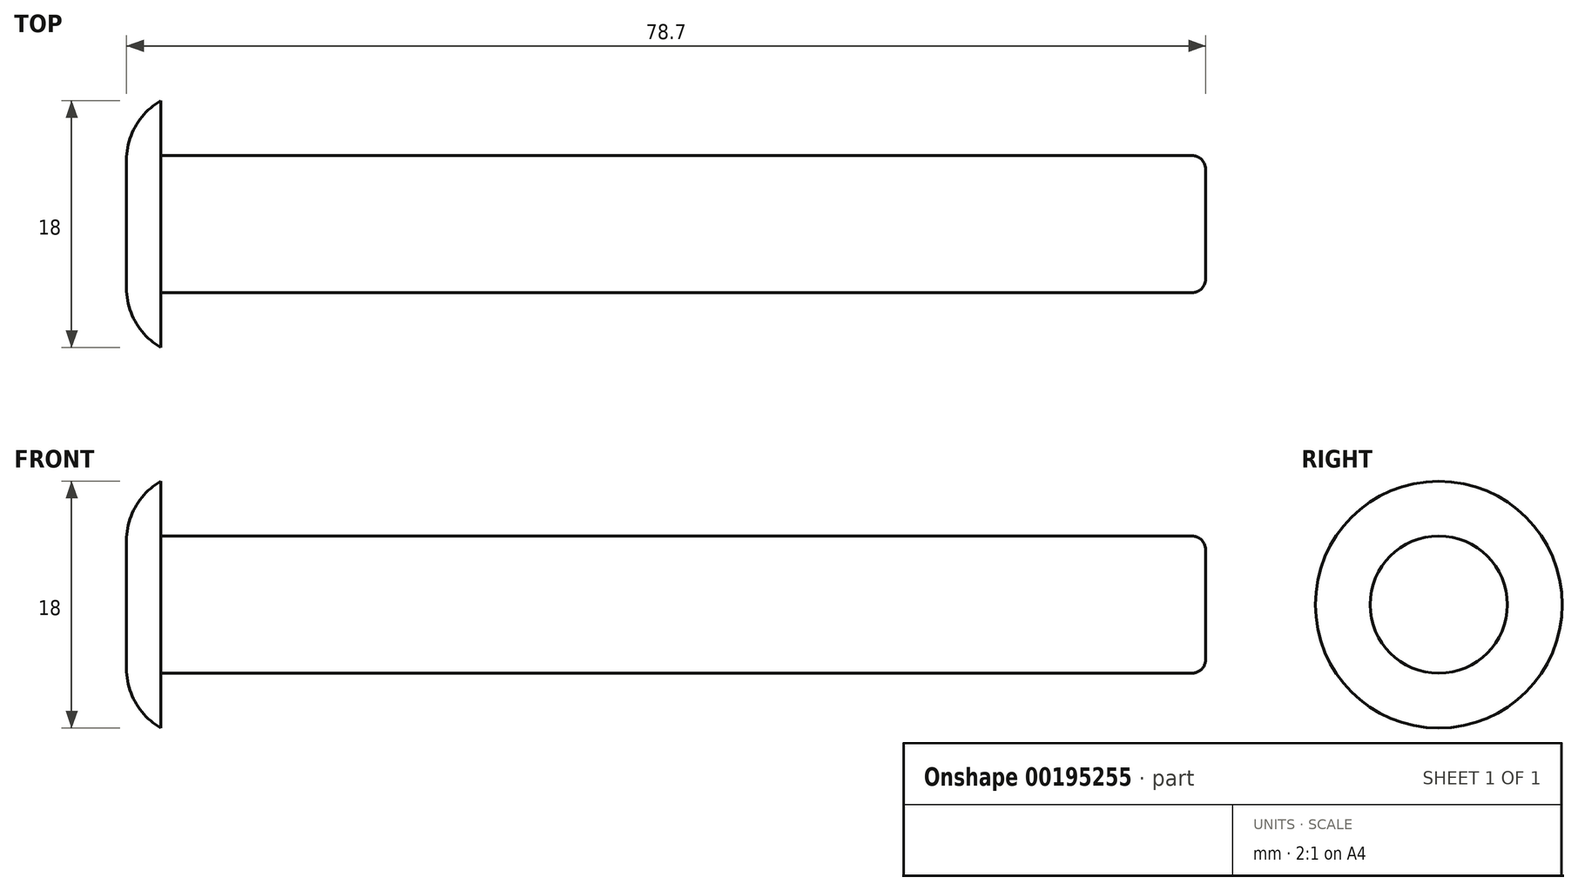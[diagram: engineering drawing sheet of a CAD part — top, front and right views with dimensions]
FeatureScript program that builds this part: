
annotation { "Feature Type Name" : "Feature", "Feature Type Description" : "" }
export const myFeature = defineFeature(function(context is Context, id is Id, definition is map)
    precondition{}
    {
        {
            var Q0;
            Q0=qCreatedBy(makeId("Right.planeOp"),FACE);
            var sketch = newSketch(context, id + "F0", { "sketchPlane" : qUnion([Q0])});
            skLineSegment(sketch, "E0", {"start": v(-18, 47.71) * mm, "end": v(-18, -27) * mm, "construction": true});
            skLineSegment(sketch, "E1", {"start": v(-18, -27) * mm, "end": v(0, -27) * mm, "construction": true});
            skLineSegment(sketch, "E2", {"start": v(0, -27) * mm, "end": v(0, -9) * mm, "construction": true});
            skLineSegment(sketch, "E3", {"start": v(0, -9) * mm, "end": v(0, 0) * mm, "construction": true});
            skCircle(sketch, "E4", {"center": v(0, 0) * mm, "radius": 9 * mm, "construction": true});
            skCircle(sketch, "E5", {"center": v(0, 0) * mm, "radius": 5 * mm});
            skSolve(sketch);
        }
        {
            var Q0;
            Q0=qCreatedBy(makeId("Right.planeOp"),FACE);
            var sketch = newSketch(context, id + "F1", { "sketchPlane" : qUnion([Q0])});
            skCircle(sketch, "E6.0", {"center": v(0, 0) * mm, "radius": 9 * mm});
            skSolve(sketch);
        }
        {
            var Q0;
            Q0 = qSketchRegion(id + "F0", true);
            extrude(context, id + "F2", {"entities" : qUnion([Q0]), "depth" : 76.2 * mm});
        }
        {
            var Q0;
            Q0 = qSketchRegion(id + "F1", true);
            extrude(context, id + "F3", {"entities" : qUnion([Q0]), "operationType" : NewBodyOperationType.ADD, "oppositeDirection" : true, "depth" : 2.5 * mm});
        }
        {
            var Q0;
            Q0=makeQuery(id+"F3.opExtrude","CAP_EDGE",EDGE,{"disambiguationData":[OSD([sQuery(id+"F1.wireOp",EDGE,"E6.0")])],"isStart":false});
            fillet(context, id + "F4", {"entities" : qUnion([Q0]), "radius" : 5 * mm, "tangentPropagation" : true, "allowEdgeOverflow" : false});
        }
        {
            var Q0;
            Q0=makeQuery(id+"F2.opExtrude","CAP_EDGE",EDGE,{"disambiguationData":[OSD([sQuery(id+"F0.wireOp",EDGE,"E5")])],"isStart":false});
            fillet(context, id + "F5", {"entities" : qUnion([Q0]), "radius" : 1 * mm, "tangentPropagation" : true, "allowEdgeOverflow" : false});
        }
    });
